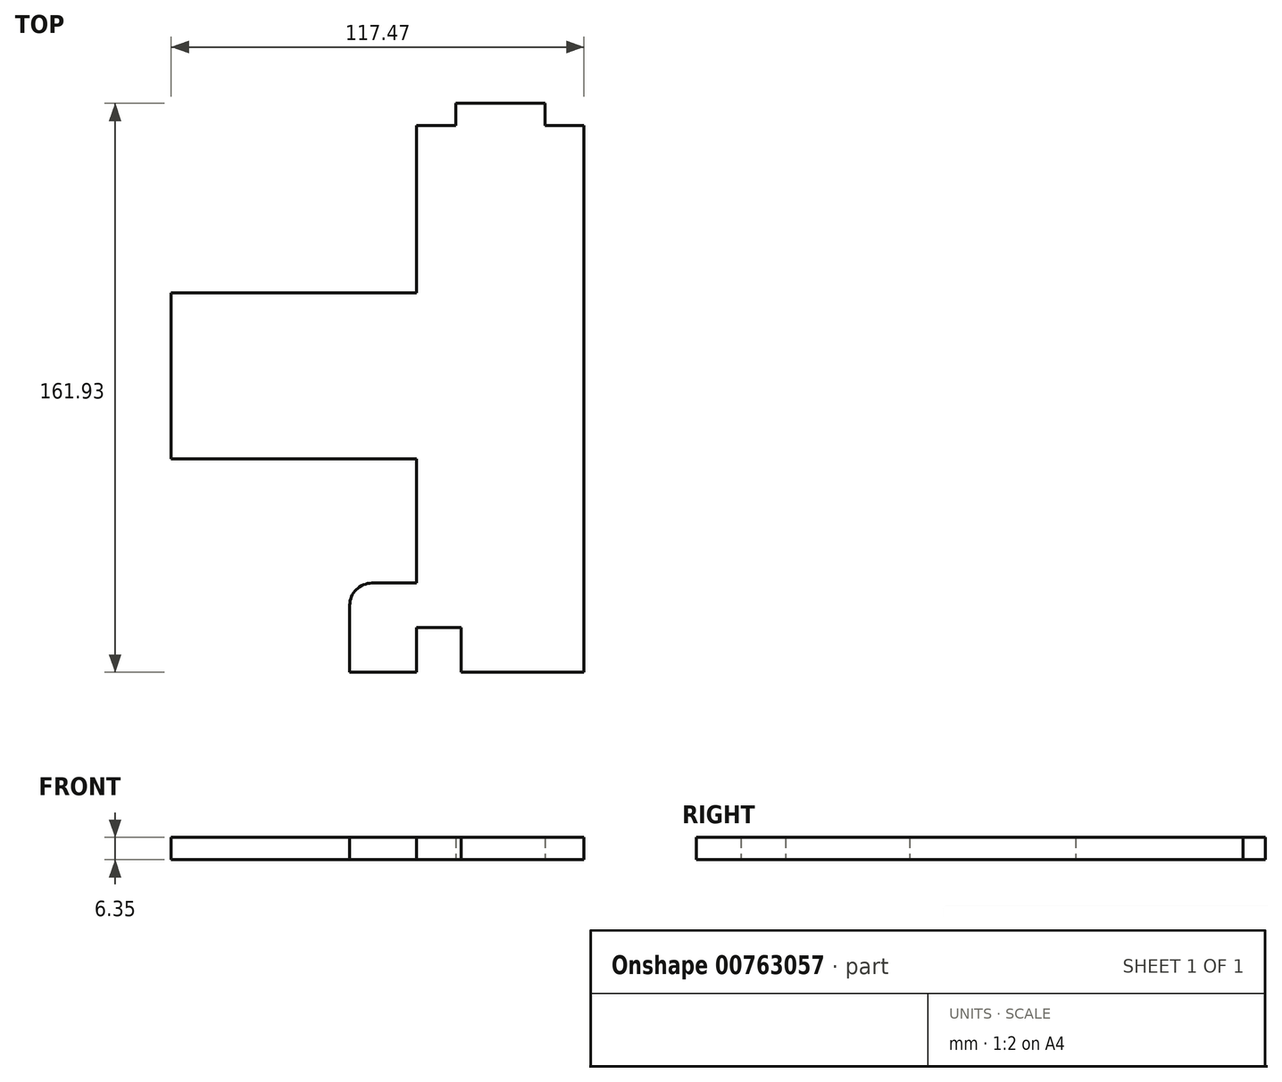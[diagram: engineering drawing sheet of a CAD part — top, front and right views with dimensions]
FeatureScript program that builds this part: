
annotation { "Feature Type Name" : "Feature", "Feature Type Description" : "" }
export const myFeature = defineFeature(function(context is Context, id is Id, definition is map)
    precondition{}
    {
        {
            var Q0;
            Q0=qCreatedBy(makeId("Top.planeOp"),FACE);
            var sketch = newSketch(context, id + "F0", { "sketchPlane" : qUnion([Q0])});
            skLineSegment(sketch, "E0", {"start": v(21.17, -220.11) * mm, "end": v(10.06, -220.11) * mm});
            skLineSegment(sketch, "E1", {"start": v(-26.45, -267.74) * mm, "end": v(-96.3, -267.74) * mm});
            skLineSegment(sketch, "E2", {"start": v(-96.3, -314.98) * mm, "end": v(-26.45, -314.98) * mm});
            skLineSegment(sketch, "E3", {"start": v(-26.45, -220.11) * mm, "end": v(-26.45, -267.74) * mm});
            skLineSegment(sketch, "E4", {"start": v(21.17, -220.11) * mm, "end": v(21.17, -375.69) * mm});
            skLineSegment(sketch, "E5", {"start": v(-13.75, -375.69) * mm, "end": v(21.17, -375.69) * mm});
            skLineSegment(sketch, "E6", {"start": v(-45.5, -356.64) * mm, "end": v(-45.5, -375.69) * mm});
            skLineSegment(sketch, "E7", {"start": v(-26.45, -362.99) * mm, "end": v(-13.75, -362.99) * mm});
            skLineSegment(sketch, "E8", {"start": v(-13.75, -375.69) * mm, "end": v(-13.75, -362.99) * mm});
            skLineSegment(sketch, "E9", {"start": v(-26.45, -350.29) * mm, "end": v(-39.15, -350.29) * mm});
            skLineSegment(sketch, "E10", {"start": v(-26.45, -375.69) * mm, "end": v(-45.5, -375.69) * mm});
            skLineSegment(sketch, "E11", {"start": v(-26.45, -362.99) * mm, "end": v(-26.45, -375.69) * mm});
            skLineSegment(sketch, "E12", {"start": v(-26.45, -314.98) * mm, "end": v(-26.45, -350.29) * mm});
            skLineSegment(sketch, "E13", {"start": v(-96.3, -267.74) * mm, "end": v(-96.3, -314.98) * mm});
            skPoint(sketch, "E14.visualSharp", {"position": v(-45.5, -350.29) * mm});
            skArc(sketch, "E14.filletArc", {"start": v(-39.15, -350.29) * mm, "mid": v(-43.64, -352.15) * mm, "end": v(-45.5, -356.64) * mm});
            skLineSegment(sketch, "E15.top", {"start": v(-15.34, -213.76) * mm, "end": v(10.06, -213.76) * mm});
            skLineSegment(sketch, "E15.left", {"start": v(-15.34, -220.11) * mm, "end": v(-15.34, -213.76) * mm});
            skLineSegment(sketch, "E15.right", {"start": v(10.06, -220.11) * mm, "end": v(10.06, -213.76) * mm});
            skLineSegment(sketch, "E16.trimOffspring", {"start": v(-15.34, -220.11) * mm, "end": v(-26.45, -220.11) * mm});
            skSolve(sketch);
        }
        {
            var Q0;
            Q0 = qSketchRegion(id + "F0", true);
            extrude(context, id + "F1", {"entities" : qUnion([Q0]), "depth" : 6.35 * mm, "offsetDistance" : 25.4 * mm});
        }
    });
